# Revit family: KNS_KK_Заглушка парапетная_IEK
name_source: partatom
category: Соединительные детали воздуховодов
units: mm (PartAtom-declared; Revit-internal decimal feet)

## family parameters
Всегда вертикально = Да
Заголовок OmniClass = Air Ductwork
На основе рабочей плоскости = Нет
Номер OmniClass = 23.75.70.14
Общий = Нет
При загрузке вырезать с полостями = Нет
Размер круглого соединителя = Использовать диаметр
Тип детали = Заглушка

## types (1)
- Стандарт
    ADSK_URL документации изделия = https://www.iek.ru
    ADSK_URL страницы изделия = https://www.iek.ru
    ADSK_Версия Revit = 2019
    ADSK_Версия семейства = 1.1
    ADSK_Группирование = Кабельные короба
    ADSK_Единица измерения = шт
    ADSK_Завод-изготовитель = IEK
    ADSK_Марка = ПРАЙМЕР
    ADSK_Материал наименование = ПВХ (PVC)
    ADSK_Материал обозначение = Пластик
    ADSK_Обозначение = ТУ 27.33.14-004-83135016-2017
    IEK_Гарантийный срок = 2 года
    IEK_Монтажная температура = -15...+60 °C
    IEK_Описание = Заглушка служит для закрытия торца кабель-канала.
    IEK_Срок службы = 25 лет
    KSI_CMa_Строительные материалы = 01.07.14
    KSI_CPr_Строительные изделия = 20.2.05.01
    URL = https://www.iek.ru
    Длина воздуховода = 25 мм
    Изготовитель = IEK
